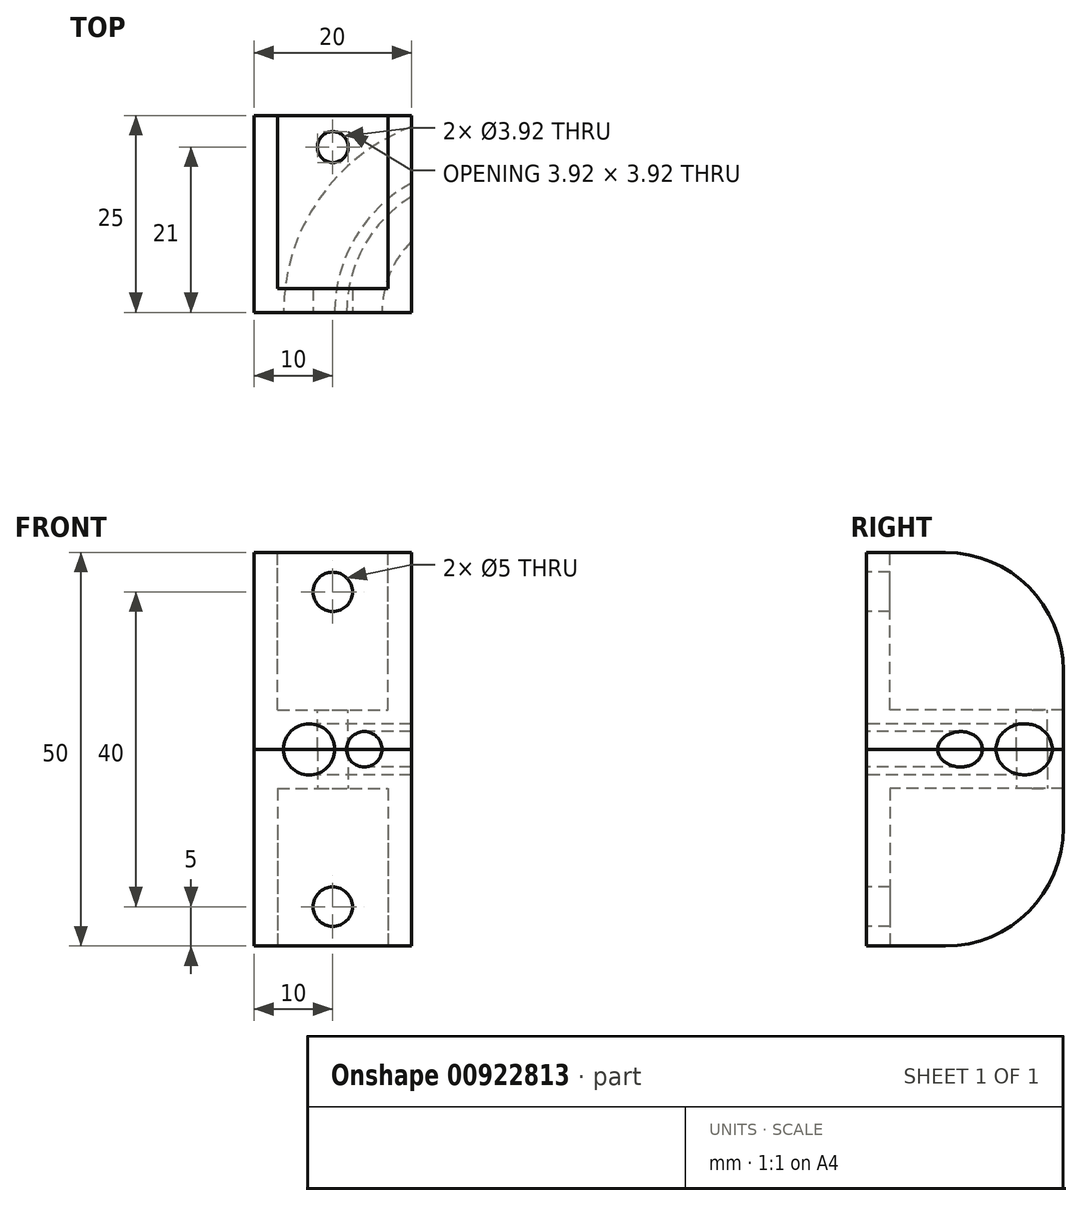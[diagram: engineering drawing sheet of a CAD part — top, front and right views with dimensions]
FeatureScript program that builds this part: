
annotation { "Feature Type Name" : "Feature", "Feature Type Description" : "" }
export const myFeature = defineFeature(function(context is Context, id is Id, definition is map)
    precondition{}
    {
        {
            var Q0;
            Q0=qCreatedBy(makeId("Top.planeOp"),FACE);
            var sketch = newSketch(context, id + "F0", { "sketchPlane" : qUnion([Q0])});
            skCircle(sketch, "E0", {"center": v(0, 0) * mm, "radius": 15 * mm});
            skCircle(sketch, "E1", {"center": v(0, 0) * mm, "radius": 22 * mm});
            skSolve(sketch);
        }
        {
            var Q0;
            Q0=qCreatedBy(makeId("Right.planeOp"),FACE);
            var sketch = newSketch(context, id + "F1", { "sketchPlane" : qUnion([Q0])});
            skCircle(sketch, "E2", {"center": v(15, 0) * mm, "radius": 2.25 * mm});
            skCircle(sketch, "E3", {"center": v(22, 0) * mm, "radius": 3.25 * mm});
            skSolve(sketch);
        }
        {
            var Q0;
            Q0=qCreatedBy(makeId("Front.planeOp"),FACE);
            var sketch = newSketch(context, id + "F2", { "sketchPlane" : qUnion([Q0])});
            skLineSegment(sketch, "E4.bottom", {"start": v(-29, -25) * mm, "end": v(-9, -25) * mm});
            skLineSegment(sketch, "E4.top", {"start": v(-29, 25) * mm, "end": v(-9, 25) * mm});
            skLineSegment(sketch, "E4.left", {"start": v(-29, -25) * mm, "end": v(-29, 25) * mm});
            skLineSegment(sketch, "E4.right", {"start": v(-9, -25) * mm, "end": v(-9, 25) * mm});
            skSolve(sketch);
        }
        {
            var Q0;
            Q0=makeQuery(id+"F2.imprint","IMPRINT",FACE,{"disambiguationData":[TD([[makeQuery(id+"F2.imprint","IMPRINT",EDGE,{"derivedFrom":sQuery(id+"F2.wireOp",EDGE,"E4.bottom")}),1.0]])]});
            extrude(context, id + "F3", {"entities" : qUnion([Q0]), "oppositeDirection" : true, "depth" : 25 * mm, "offsetDistance" : 25 * mm});
        }
        {
            var Q0;
            Q0=qCreatedBy(makeId("Front.planeOp"),FACE);
            var sketch = newSketch(context, id + "F4", { "sketchPlane" : qUnion([Q0])});
            skLineSegment(sketch, "E5.bottom", {"start": v(-26, 5) * mm, "end": v(-12, 5) * mm});
            skLineSegment(sketch, "E5.top", {"start": v(-26, 26) * mm, "end": v(-12, 26) * mm});
            skLineSegment(sketch, "E5.left", {"start": v(-26, 5) * mm, "end": v(-26, 26) * mm});
            skLineSegment(sketch, "E5.right", {"start": v(-12, 5) * mm, "end": v(-12, 26) * mm});
            skSolve(sketch);
        }
        {
            var Q0;
            Q0 = qSketchRegion(id + "F4", true);
            extrude(context, id + "F5", {"entities" : qUnion([Q0]), "operationType" : NewBodyOperationType.REMOVE, "endBound" : BoundingType.THROUGH_ALL, "oppositeDirection" : true, "depth" : 2 * mm, "offsetDistance" : 25 * mm, "hasSecondDirection" : true, "secondDirectionOppositeDirection" : true, "secondDirectionDepth" : 3 * mm});
        }
        {
            var Q0;
            Q0=makeQuery(id+"F1.imprint","IMPRINT",FACE,{"disambiguationData":[TD([[makeQuery(id+"F1.imprint","IMPRINT",EDGE,{"derivedFrom":sQuery(id+"F1.wireOp",EDGE,"E3")}),1.0]])]});
            var Q1;
            Q1=sQuery(id+"F0.wireOp",EDGE,"E1");
            revolve(context, id + "F6", {"operationType" : NewBodyOperationType.REMOVE, "surfaceOperationType" : NewSurfaceOperationType.NEW, "entities" : qUnion([Q0]), "axis" : qUnion([Q1]), "revolveType" : RevolveType.ONE_DIRECTION, "angle" : 90 * degree});
        }
        {
            var Q0;
            Q0=makeQuery(id+"F1.imprint","IMPRINT",FACE,{"disambiguationData":[TD([[makeQuery(id+"F1.imprint","IMPRINT",EDGE,{"derivedFrom":sQuery(id+"F1.wireOp",EDGE,"E2")}),1.0]])]});
            var Q1;
            Q1=sQuery(id+"F0.wireOp",EDGE,"E0");
            revolve(context, id + "F7", {"operationType" : NewBodyOperationType.REMOVE, "surfaceOperationType" : NewSurfaceOperationType.NEW, "entities" : qUnion([Q0]), "axis" : qUnion([Q1]), "revolveType" : RevolveType.ONE_DIRECTION, "angle" : 90 * degree});
        }
        {
            var Q0;
            Q0=qCreatedBy(makeId("Front.planeOp"),FACE);
            var sketch = newSketch(context, id + "F8", { "sketchPlane" : qUnion([Q0])});
            skCircle(sketch, "E6", {"center": v(-19, 20) * mm, "radius": 2.5 * mm});
            skSolve(sketch);
        }
        {
            var Q0;
            Q0 = qSketchRegion(id + "F8", true);
            extrude(context, id + "F9", {"entities" : qUnion([Q0]), "operationType" : NewBodyOperationType.REMOVE, "oppositeDirection" : true, "depth" : 25 * mm, "offsetDistance" : 25 * mm});
        }
        {
            var Q0;
            Q0=qCreatedBy(makeId("Top.planeOp"),FACE);
            var sketch = newSketch(context, id + "F10", { "sketchPlane" : qUnion([Q0])});
            skCircle(sketch, "E7", {"center": v(-19, 21) * mm, "radius": 1.96 * mm});
            skSolve(sketch);
        }
        {
            var Q0;
            Q0=makeQuery(id+"F10.imprint","IMPRINT",FACE,{"disambiguationData":[TD([[makeQuery(id+"F10.imprint","IMPRINT",EDGE,{"derivedFrom":sQuery(id+"F10.wireOp",EDGE,"E7")}),1.0]])]});
            extrude(context, id + "F11", {"entities" : qUnion([Q0]), "operationType" : NewBodyOperationType.REMOVE, "oppositeDirection" : true, "depth" : 25 * mm, "offsetDistance" : 25 * mm, "hasSecondDirection" : true, "secondDirectionOppositeDirection" : false, "secondDirectionDepth" : 25 * mm});
        }
        {
            var Q0;
            Q0=qCreatedBy(makeId("Front.planeOp"),FACE);
            var sketch = newSketch(context, id + "F12", { "sketchPlane" : qUnion([Q0])});
            skLineSegment(sketch, "E8.bottom", {"start": v(-3, 0) * mm, "end": v(-38.9, 0) * mm});
            skLineSegment(sketch, "E8.top", {"start": v(-3, -25.54) * mm, "end": v(-38.9, -25.54) * mm});
            skLineSegment(sketch, "E8.left", {"start": v(-3, 0) * mm, "end": v(-3, -25.54) * mm});
            skLineSegment(sketch, "E8.right", {"start": v(-38.9, 0) * mm, "end": v(-38.9, -25.54) * mm});
            skSolve(sketch);
        }
        {
            var Q0;
            Q0 = qSketchRegion(id + "F12", true);
            extrude(context, id + "F13", {"entities" : qUnion([Q0]), "operationType" : NewBodyOperationType.REMOVE, "oppositeDirection" : true, "depth" : 25 * mm, "offsetDistance" : 25 * mm});
        }
        {
            var Q0;
            {var subQ0=sQuery(id+"F2.wireOp",EDGE,"E4.right");var subQ1=sQuery(id+"F2.wireOp",EDGE,"E4.top");Q0=makeQuery(id+"F5.boolean.opBoolean","SPLIT",EDGE,{"disambiguationData":[TD([makeQuery(id+"F3.opExtrude","SWEPT_FACE",FACE,{"disambiguationData":[OSD([subQ0])]})])],"derivedFrom":makeQuery(id+"F3.opExtrude","CAP_EDGE",EDGE,{"disambiguationData":[OSD([subQ1])],"isStart":false})});}
            var Q1;
            {var subQ0=sQuery(id+"F2.wireOp",EDGE,"E4.left");var subQ1=sQuery(id+"F2.wireOp",EDGE,"E4.top");Q1=makeQuery(id+"F5.boolean.opBoolean","SPLIT",EDGE,{"disambiguationData":[TD([makeQuery(id+"F3.opExtrude","SWEPT_FACE",FACE,{"disambiguationData":[OSD([subQ0])]})])],"derivedFrom":makeQuery(id+"F3.opExtrude","CAP_EDGE",EDGE,{"disambiguationData":[OSD([subQ1])],"isStart":false})});}
            fillet(context, id + "F14", {"entities" : qUnion([Q0, Q1]), "radius" : 15 * mm, "tangentPropagation" : true, "allowEdgeOverflow" : false});
        }
        {
            var Q0;
            Q0=makeQuery(id+"F3.opExtrude","SWEPT_BODY",BODY,{"disambiguationData":[OSD([sQuery(id+"F2.wireOp",EDGE,"E4.bottom"),sQuery(id+"F2.wireOp",EDGE,"E4.top"),sQuery(id+"F2.wireOp",EDGE,"E4.left"),sQuery(id+"F2.wireOp",EDGE,"E4.right")])]});
            var Q1;
            Q1=qCreatedBy(makeId("Top.planeOp"),FACE);
            mirror(context, id + "F15", {"entities" : qUnion([Q0]), "mirrorPlane" : qUnion([Q1])});
        }
    });
